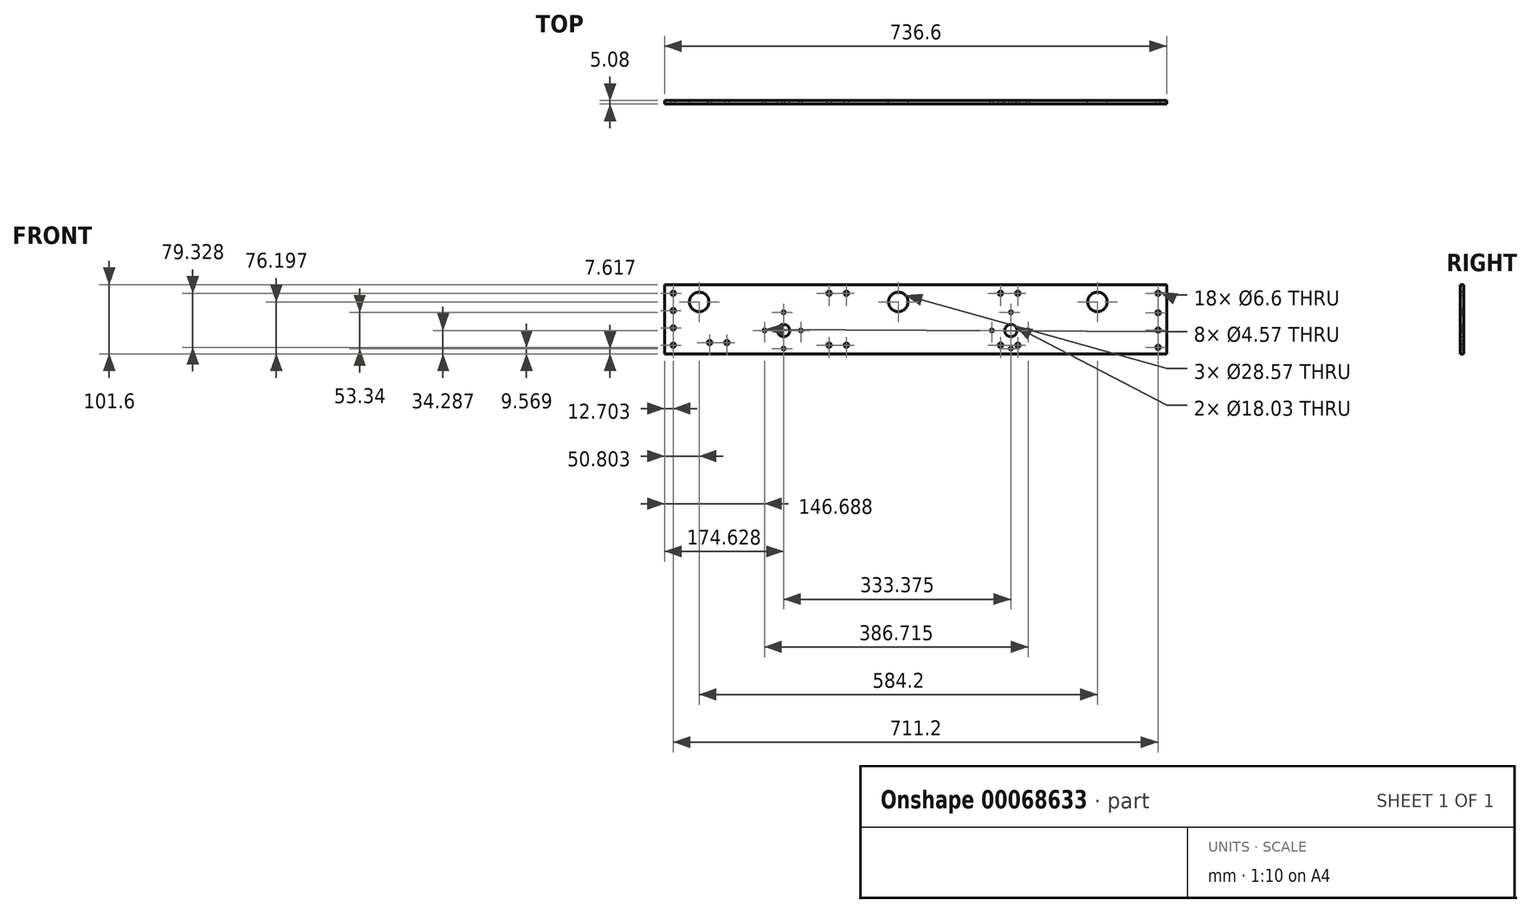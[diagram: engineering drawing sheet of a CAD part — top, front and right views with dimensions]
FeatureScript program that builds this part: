
annotation { "Feature Type Name" : "Feature", "Feature Type Description" : "" }
export const myFeature = defineFeature(function(context is Context, id is Id, definition is map)
    precondition{}
    {
        {
            var Q0;
            Q0=qCreatedBy(makeId("Front.planeOp"),FACE);
            var sketch = newSketch(context, id + "F0", { "sketchPlane" : qUnion([Q0])});
            skLineSegment(sketch, "E0.bottom", {"start": v(-206.3, 50.94) * mm, "end": v(530.3, 50.94) * mm});
            skLineSegment(sketch, "E0.top", {"start": v(-206.3, -50.66) * mm, "end": v(530.3, -50.66) * mm});
            skLineSegment(sketch, "E0.left", {"start": v(-206.3, 50.94) * mm, "end": v(-206.3, -50.66) * mm});
            skLineSegment(sketch, "E0.right", {"start": v(530.3, 50.94) * mm, "end": v(530.3, -50.66) * mm});
            skCircle(sketch, "E1", {"center": v(-193.6, 38.24) * mm, "radius": 3.3 * mm});
            skCircle(sketch, "E2", {"center": v(-193.6, 12.84) * mm, "radius": 3.3 * mm});
            skCircle(sketch, "E3", {"center": v(-193.6, -12.56) * mm, "radius": 3.3 * mm});
            skCircle(sketch, "E4", {"center": v(-193.6, -37.96) * mm, "radius": 3.3 * mm});
            skCircle(sketch, "E5", {"center": v(-140.27, -34.15) * mm, "radius": 3.3 * mm});
            skCircle(sketch, "E6", {"center": v(-114.87, -34.15) * mm, "radius": 3.3 * mm});
            skCircle(sketch, "E7", {"center": v(35, -37.96) * mm, "radius": 3.3 * mm});
            skCircle(sketch, "E8", {"center": v(60.4, -37.96) * mm, "radius": 3.3 * mm});
            skCircle(sketch, "E9", {"center": v(286.45, -37.96) * mm, "radius": 3.3 * mm});
            skCircle(sketch, "E10", {"center": v(311.85, -37.96) * mm, "radius": 3.3 * mm});
            skCircle(sketch, "E11", {"center": v(286.45, 38.24) * mm, "radius": 3.3 * mm});
            skCircle(sketch, "E12", {"center": v(311.85, 38.24) * mm, "radius": 3.3 * mm});
            skCircle(sketch, "E13.MirrorC", {"center": v(517.6, 38.24) * mm, "radius": 3.3 * mm});
            skCircle(sketch, "E14.MirrorC", {"center": v(517.6, 9.7) * mm, "radius": 3.3 * mm});
            skCircle(sketch, "E15.MirrorC", {"center": v(517.6, -15.7) * mm, "radius": 3.3 * mm});
            skCircle(sketch, "E16.MirrorC", {"center": v(517.6, -41.1) * mm, "radius": 3.3 * mm});
            skLineSegment(sketch, "E17", {"start": v(-206.3, 0.14) * mm, "end": v(-181.73, 0.14) * mm});
            skCircle(sketch, "E18.MirrorC", {"center": v(60.4, 38.24) * mm, "radius": 3.3 * mm});
            skCircle(sketch, "E19.MirrorC", {"center": v(35, 38.24) * mm, "radius": 3.3 * mm});
            skCircle(sketch, "E20", {"center": v(428.7, 25.54) * mm, "radius": 14.29 * mm});
            skCircle(sketch, "E21", {"center": v(136.6, 25.54) * mm, "radius": 14.29 * mm});
            skCircle(sketch, "E22", {"center": v(-31.68, -43.04) * mm, "radius": 2.29 * mm});
            skCircle(sketch, "E23", {"center": v(-31.68, 10.3) * mm, "radius": 2.29 * mm});
            skCircle(sketch, "E24", {"center": v(-6.28, -16.37) * mm, "radius": 2.29 * mm});
            skCircle(sketch, "E25", {"center": v(-59.62, -16.37) * mm, "radius": 2.29 * mm});
            skCircle(sketch, "E26", {"center": v(-31.68, -16.37) * mm, "radius": 9.02 * mm});
            skCircle(sketch, "E27", {"center": v(-155.5, 25.54) * mm, "radius": 14.29 * mm});
            skCircle(sketch, "E28", {"center": v(301.7, -16.37) * mm, "radius": 9.02 * mm});
            skCircle(sketch, "E29", {"center": v(273.75, -16.37) * mm, "radius": 2.29 * mm});
            skCircle(sketch, "E30", {"center": v(301.7, -43.04) * mm, "radius": 2.29 * mm});
            skCircle(sketch, "E31", {"center": v(327.1, -16.37) * mm, "radius": 2.29 * mm});
            skCircle(sketch, "E32", {"center": v(301.7, 10.3) * mm, "radius": 2.29 * mm});
            skSolve(sketch);
        }
        {
            var Q0;
            {var subQ3=sQuery(id+"F0.wireOp",EDGE,"E0.bottom");Q0=makeQuery(id+"F0.imprint","IMPRINT",FACE,{"disambiguationData":[TD([[makeQuery(id+"F0.imprint","IMPRINT",EDGE,{"derivedFrom":subQ3}),-1.0]])]});}
            extrude(context, id + "F1", {"entities" : qUnion([Q0]), "depth" : 5.08 * mm});
        }
    });
